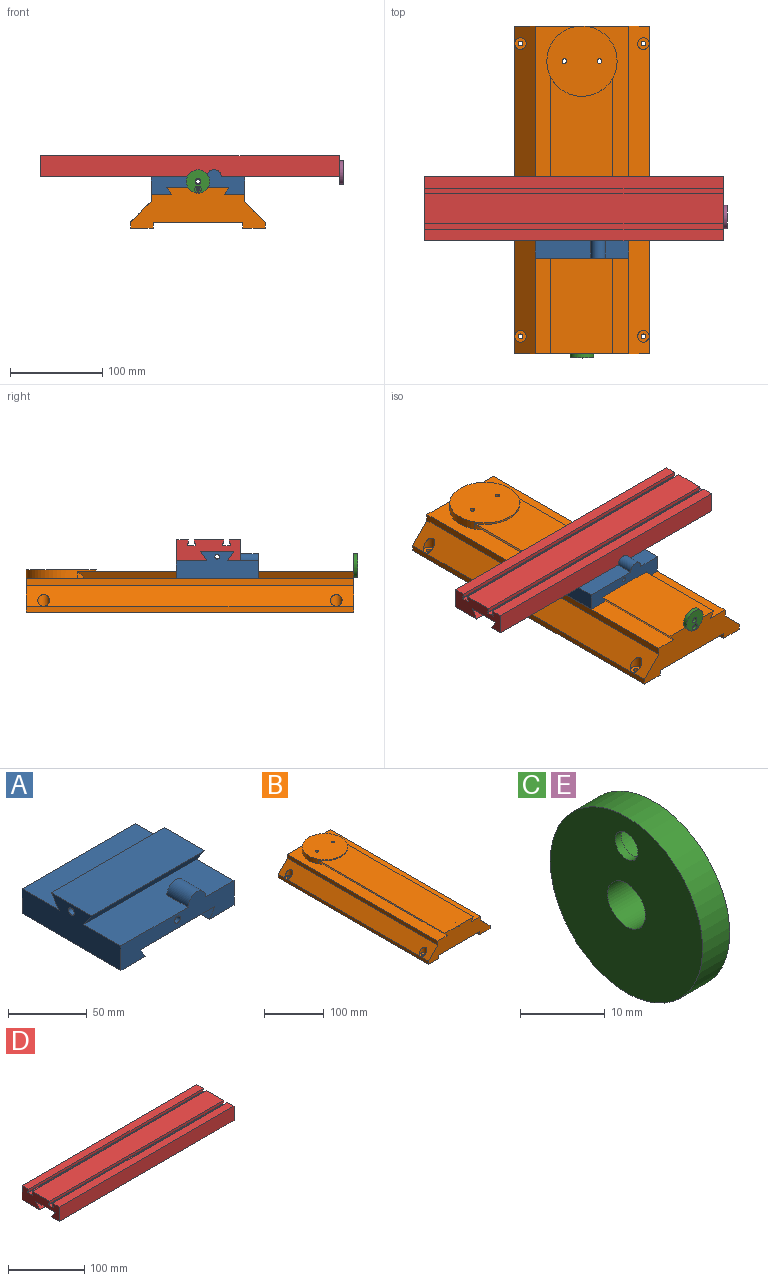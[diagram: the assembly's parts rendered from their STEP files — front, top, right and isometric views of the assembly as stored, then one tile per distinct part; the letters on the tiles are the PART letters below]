
ASSEMBLY  parts=5 mates=6
PART A: 20 faces, bbox 101.6x88.9x29.2 mm
  f0: cylinder r=2.55mm len=38.1mm, axis (0,-1,0), area 611.1mm2, adj f10,f19
  f1: plane 101.6x33.34mm, normal (0,0,1), area 3084.7mm2, adj f2,f8,f10,f12,f15,f16
  f2: plane 88.9x29.21mm, normal (-1,0,0), area 1969.8mm2, adj f1,f3,f9,f10,f11,f12,f13,f14
  f3: plane 88.9x22.29mm, normal (0,0,-1), area 1982mm2, adj f2,f4,f10,f11
  f4: plane 88.9x7.49mm, normal (0.82,0,0.57), area 808.3mm2, adj f3,f5,f10,f11
  f5: plane 88.9x67.31mm, normal (0,0,-1), area 5983.9mm2, adj f4,f6,f10,f11
  f6: plane 88.9x7.49mm, normal (-0.82,0,0.57), area 808.3mm2, adj f5,f7,f10,f11
  f7: plane 88.9x22.29mm, normal (0,0,-1), area 1982mm2, adj f6,f8,f10,f11
  f8: plane 88.9x29.21mm, normal (1,0,0), area 1969.8mm2, adj f1,f7,f9,f10,f11,f12,f13,f14
  f9: plane 101.6x33.34mm, normal (0,0,1), area 3387.1mm2, adj f2,f8,f11,f13
  f10: plane 101.6x26.99mm, normal (0,-1,0), area 1548.2mm2, adj f0,f1,f2,f3,f4,f5,f6,f7
  f11: plane 101.6x19.05mm, normal (0,1,0), area 1420.2mm2, adj f2,f3,f4,f5,f6,f7,f8,f9
  f12: plane 101.6x10.16mm, normal (0,-0.82,-0.57), area 1252.5mm2, adj f1,f2,f8,f14
  f13: plane 101.6x10.16mm, normal (0,0.82,-0.57), area 1252.5mm2, adj f2,f8,f9,f14
  f14: plane 101.6x36.19mm, normal (0,0,1), area 3677mm2, adj f2,f8,f12,f13
  f15: cylinder r=7.94mm len=19.05mm, axis (0,-1,0), area 475mm2, adj f1,f10,f16
  f16: plane 15.88x7.94mm, normal (0,1,0), area 99mm2, adj f1,f15
  f17: cylinder r=2.55mm len=101.6mm, axis (1,0,0), area 1629.6mm2, adj f2,f8
  f18: cylinder r=3.97mm len=50.8mm, axis (0,1,0), area 1266.8mm2, adj f11,f19
  f19: plane 7.94x7.94mm, normal (0,1,0), area 29mm2, adj f0,f18
PART B: 37 faces, bbox 146.1x355.6x46.1 mm
  f0: plane 146.05x36.58mm, normal (0,1,0), area 3876mm2, adj f1,f5,f6,f7,f8,f9,f10,f11
  f1: plane 355.6x50.8mm, normal (0,0,1), area 7707.7mm2, adj f0,f2,f10,f17,f30
  f2: plane 299.64x7.49mm, normal (0.82,0,-0.57), area 2687.8mm2, adj f1,f3,f17,f30
  f3: plane 299.64x67.31mm, normal (0,0,1), area 19197.9mm2, adj f2,f4,f17,f30
  f4: plane 299.64x7.49mm, normal (-0.82,0,-0.57), area 2687.8mm2, adj f3,f11,f17,f31
  f5: plane 355.6x97.28mm, normal (0,0,-1), area 34552.5mm2, adj f0,f6,f16,f17,f33,f34
  f6: plane 355.6x6.35mm, normal (-1,0,0), area 2258.1mm2, adj f0,f5,f7,f17
  f7: plane 355.6x24.38mm, normal (0,0,-1), area 8630mm2, adj f0,f6,f8,f17,f27,f28
  f8: plane 355.6x6.35mm, normal (1,0,0), area 2258.1mm2, adj f0,f7,f9,f17
  f9: plane 355.6x22.29mm, normal (0.71,0,0.71), area 10834mm2, adj f0,f8,f10,f17,f21,f23
  f10: plane 355.6x7.94mm, normal (1,0,0), area 2822.6mm2, adj f0,f1,f9,f17
  f11: plane 355.6x50.8mm, normal (0,0,1), area 7707.7mm2, adj f0,f4,f12,f17,f30,f31
  f12: plane 355.6x7.94mm, normal (-1,0,0), area 2822.6mm2, adj f0,f11,f13,f17
  f13: plane 355.6x22.29mm, normal (-0.71,0,0.71), area 10834mm2, adj f0,f12,f14,f17,f18,f24
  f14: plane 355.6x6.35mm, normal (-1,0,0), area 2258.1mm2, adj f0,f13,f15,f17
  f15: plane 355.6x24.38mm, normal (0,0,-1), area 8630mm2, adj f0,f14,f16,f17,f26,f29
  f16: plane 355.6x6.35mm, normal (1,0,0), area 2258.1mm2, adj f0,f5,f15,f17
  f17: plane 146.05x44.07mm, normal (0,-1,0), area 4337.8mm2, adj f1,f2,f3,f4,f5,f6,f7,f8
  f18: cylinder r=6.35mm len=12.83mm, axis (0,0,-1), area 254.1mm2, adj f13,f19
  f19: plane 12.7x12.7mm, normal (0,0,1), area 106.2mm2, adj f18,f26
  f20: plane 12.7x12.7mm, normal (0,0,1), area 106.2mm2, adj f21,f27
  f21: cylinder r=6.35mm len=12.83mm, axis (0,0,-1), area 254.1mm2, adj f9,f20
  f22: plane 12.7x12.7mm, normal (0,0,1), area 106.2mm2, adj f23,f28
  f23: cylinder r=6.35mm len=12.83mm, axis (0,0,-1), area 254.1mm2, adj f9,f22
  f24: cylinder r=6.35mm len=12.83mm, axis (0,0,-1), area 254.1mm2, adj f13,f25
  f25: plane 12.7x12.7mm, normal (0,0,1), area 106.2mm2, adj f24,f29
  f26: cylinder r=2.55mm len=6.35mm, axis (0,0,1), area 101.8mm2, adj f15,f19
  f27: cylinder r=2.55mm len=6.35mm, axis (0,0,1), area 101.8mm2, adj f7,f20
  f28: cylinder r=2.55mm len=6.35mm, axis (0,0,1), area 101.8mm2, adj f7,f22
  f29: cylinder r=2.55mm len=6.35mm, axis (0,0,1), area 101.8mm2, adj f15,f25
  f30: cylinder r=38.1mm len=76.2mm, axis (0,0,-1), area 1697.7mm2, adj f1,f2,f3,f11,f31,f32
  f31: cylinder r=38.1mm len=7.49mm, axis (0,0,-1), area 35.9mm2, adj f4,f11,f30
  f32: plane 76.2x76.2mm, normal (0,0,1), area 4519.4mm2, adj f30,f33,f34
  f33: cylinder r=2.55mm len=39.75mm, axis (0,0,1), area 637.6mm2, adj f5,f32
  f34: cylinder r=2.55mm len=39.75mm, axis (0,0,1), area 637.6mm2, adj f5,f32
  f35: cone r=0mm half-angle=59deg, axis (0,-1,0), area 4.7mm2, adj f36
  f36: cylinder r=1.13mm len=12.7mm, axis (0,-1,0), area 90.2mm2, adj f17,f35
PART C: 7 faces, bbox 4.5x25.4x25.4 mm
  f0: cylinder r=12.7mm len=25.4mm, axis (-1,0,0), area 361.8mm2, adj f2,f3
  f1: cylinder r=3.15mm len=6.3mm, axis (-1,0,0), area 89.7mm2, adj f2,f3
  f2: plane 25.4x25.4mm, normal (1,0,0), area 435.5mm2, adj f0,f1,f6
  f3: plane 25.4x25.4mm, normal (-1,0,0), area 464.2mm2, adj f0,f1,f4
  f4: cylinder r=1.9mm len=3.8mm, axis (1,0,0), area 12.3mm2, adj f3,f5
  f5: plane 7.14x7.14mm, normal (1,0,0), area 28.8mm2, adj f4,f6
  f6: cylinder r=3.57mm len=7.14mm, axis (1,0,0), area 78.7mm2, adj f2,f5
PART D: 28 faces, bbox 323.9x69.1x22.9 mm
  f0: plane 323.85x12.19mm, normal (0,0,1), area 3948.4mm2, adj f2,f3,f9,f20
  f1: plane 323.85x32mm, normal (0,0,1), area 10364.5mm2, adj f2,f3,f18,f21
  f2: plane 69.09x22.86mm, normal (1,0,0), area 1185.8mm2, adj f0,f1,f4,f5,f6,f7,f8,f9
  f3: plane 69.09x22.86mm, normal (-1,0,0), area 1191.5mm2, adj f0,f1,f4,f5,f6,f7,f8,f9
  f4: plane 323.85x14.29mm, normal (0,0,-1), area 4627mm2, adj f2,f3,f5,f11
  f5: plane 323.85x10.16mm, normal (0,0.82,0.57), area 3992.5mm2, adj f2,f3,f4,f6
  f6: plane 323.85x36.19mm, normal (0,0,-1), area 11720.3mm2, adj f2,f3,f5,f7
  f7: plane 323.85x10.16mm, normal (0,-0.82,0.57), area 3992.5mm2, adj f2,f3,f6,f8
  f8: plane 323.85x32.58mm, normal (0,0,-1), area 10549.6mm2, adj f2,f3,f7,f9
  f9: plane 323.85x22.86mm, normal (0,1,0), area 7403.2mm2, adj f0,f2,f3,f8
  f10: plane 323.85x12.19mm, normal (0,0,1), area 3948.4mm2, adj f2,f3,f11,f12
  f11: plane 323.85x22.86mm, normal (0,-1,0), area 7403.2mm2, adj f2,f3,f4,f10
  f12: plane 323.85x4.06mm, normal (0,1,0), area 1316.1mm2, adj f2,f3,f10,f13
  f13: plane 323.85x1.14mm, normal (0,0,-1), area 370.2mm2, adj f2,f3,f12,f14
  f14: plane 323.85x2.29mm, normal (0,1,0), area 740.3mm2, adj f2,f3,f13,f15
  f15: plane 323.85x8.64mm, normal (0,0,1), area 2796.8mm2, adj f2,f3,f14,f16
  f16: plane 323.85x2.29mm, normal (0,-1,0), area 740.3mm2, adj f2,f3,f15,f17
  f17: plane 323.85x1.14mm, normal (0,0,-1), area 370.2mm2, adj f2,f3,f16,f18
  f18: plane 323.85x4.06mm, normal (0,-1,0), area 1316.1mm2, adj f1,f2,f3,f17
  f19: plane 323.85x1.14mm, normal (0,0,-1), area 370.2mm2, adj f2,f3,f20,f25
  f20: plane 323.85x4.06mm, normal (0,-1,0), area 1316.1mm2, adj f0,f2,f3,f19
  f21: plane 323.85x4.06mm, normal (0,1,0), area 1316.1mm2, adj f1,f2,f3,f22
  f22: plane 323.85x1.14mm, normal (0,0,-1), area 370.2mm2, adj f2,f3,f21,f23
  f23: plane 323.85x2.29mm, normal (0,1,0), area 740.3mm2, adj f2,f3,f22,f24
  f24: plane 323.85x8.64mm, normal (0,0,1), area 2796.8mm2, adj f2,f3,f23,f25
  f25: plane 323.85x2.29mm, normal (0,-1,0), area 740.3mm2, adj f2,f3,f19,f24
  f26: cone r=0mm half-angle=59deg, axis (1,0,0), area 6.7mm2, adj f27
  f27: cylinder r=1.35mm len=12.7mm, axis (1,0,0), area 107.9mm2, adj f2,f26
PART E: same geometry as C
PLACE A t=(0,-207.41,0)mm
PLACE B t=(0,-177.8,0)mm
PLACE C rot(axis=(0.71,-0.71,0),180deg) t=(0,-193.68,111.07)mm
PLACE D t=(-8.72,-207.41,0)mm
PLACE E t=(-8.72,-207.41,0)mm
MATE planar A.f3 <-> B.f11  axis (0,0,-1) through (-39.65,-207.41,36.58)mm
MATE fastened B.f35 <-> C.f4  axis (0,-1,0) through (0,-355.6,42.11)mm
MATE planar A.f6 <-> B.f2  axis (-0.82,0,0.57) through (31.08,-207.41,40.32)mm
MATE planar D.f8 <-> A.f9  axis (0,0,-1) through (-8.72,-180.01,55.63)mm
MATE planar D.f7 <-> A.f13  axis (0,-0.82,0.57) through (-8.72,-192.81,60.71)mm
MATE fastened D.f26 <-> E.f4  axis (1,0,0) through (153.21,-207.41,68.96)mm
